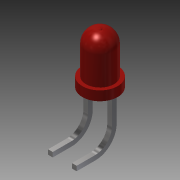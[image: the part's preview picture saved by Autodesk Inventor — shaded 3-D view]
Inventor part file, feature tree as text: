
AUTODESK INVENTOR PART (.ipt)
format: ipt  version: 2014 SP1 (Build 180222100, 222)  size: 135,168 bytes
history: native  units: mm
features: sketch x4, extrude x2, fillet x1, sweep x1
ambient origin geometry x8: Origin, YZ Plane, XZ Plane, XY Plane, X Axis, Y Axis, Z Axis, Center Point
bodies: Solid1 (feature_tree)
feature tree (8):
  extrude  "Extrusion1"  Depth=1.5mm TaperAngle=0.0deg
  fillet  "Fillet1"  Radius=1.5mm
  extrude  "Extrusion2"  Depth=1.0mm TaperAngle=0.0deg
  sweep  "Sweep1"
  sketch  "Sketch1"  dims[d0=3.0mm d1=4.49mm d2=0.0mm d3=1.5mm]
  sketch  "Sketch2"  dims[d4=3.75mm d5=1.0mm d6=0.0mm]
  sketch  "Sketch3"  dims[d7=0.5mm d8=0.5mm]
  sketch  "Sketch4"  dims[d9=0.5mm d10=0.5mm d11=0.25mm d12=0.25mm d13=1.02mm d14=1.02mm d16=4.0mm d17=5.25mm d18=2.0mm d19=1.875mm d20=0.0mm d21=0.5mm]
